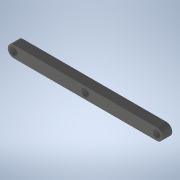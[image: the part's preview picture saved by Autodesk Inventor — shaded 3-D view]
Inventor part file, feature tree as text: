
AUTODESK INVENTOR PART (.ipt)
format: ipt  version: 2022 (Build 260153000, 153)  size: 121,856 bytes
history: native  units: mm
features: extrude x3, sketch x2, plane x1, fillet x1, mirror x1
ambient origin geometry x8: Origin, YZ Plane, XZ Plane, XY Plane, X Axis, Y Axis, Z Axis, Center Point
bodies: Solid1 (feature_tree)
feature tree (8):
  sketch  "Sketch1"  dims[d11=180.0mm d12=10.0mm d13=0.0mm]
  plane  "Work Plane1"
  extrude  "Extrusion3"  Depth=10.0mm TaperAngle=0.0deg
  extrude  "Extrusion4"  Depth=10.0mm TaperAngle=0.0deg
  fillet  "Fillet3"  Radius=6.0mm
  extrude  "Extrusion6"  Depth=10.0mm
  mirror  "Mirror2"
  sketch  "Sketch4"  dims[d14=12.0mm d15=10.0mm d16=0.0mm d17=6.0mm d22=80.0mm d23=8.0mm d24=10.0mm d25=0.0mm]
